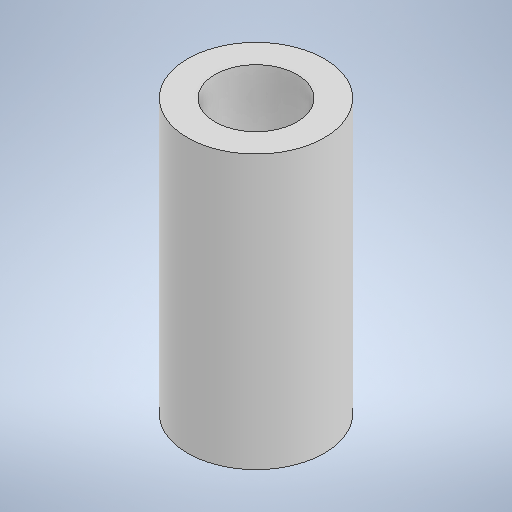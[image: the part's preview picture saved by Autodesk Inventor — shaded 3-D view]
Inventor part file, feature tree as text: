
AUTODESK INVENTOR PART (.ipt)
format: ipt  version: 2025.1 (Build 291241000, 241)  size: 257,536 bytes
history: native  units: mm
features: extrude x1, sketch x1
ambient origin geometry x8: Origin, YZ Plane, XZ Plane, XY Plane, X Axis, Y Axis, Z Axis, Center Point
bodies: Solid1 (feature_tree)
feature tree (2):
  extrude  "Extrusion1"  Depth=10.0mm
  sketch  "Sketch1"  dims[d0=5.0mm d1=3.0mm d2=10.0mm d3=0.0mm]
